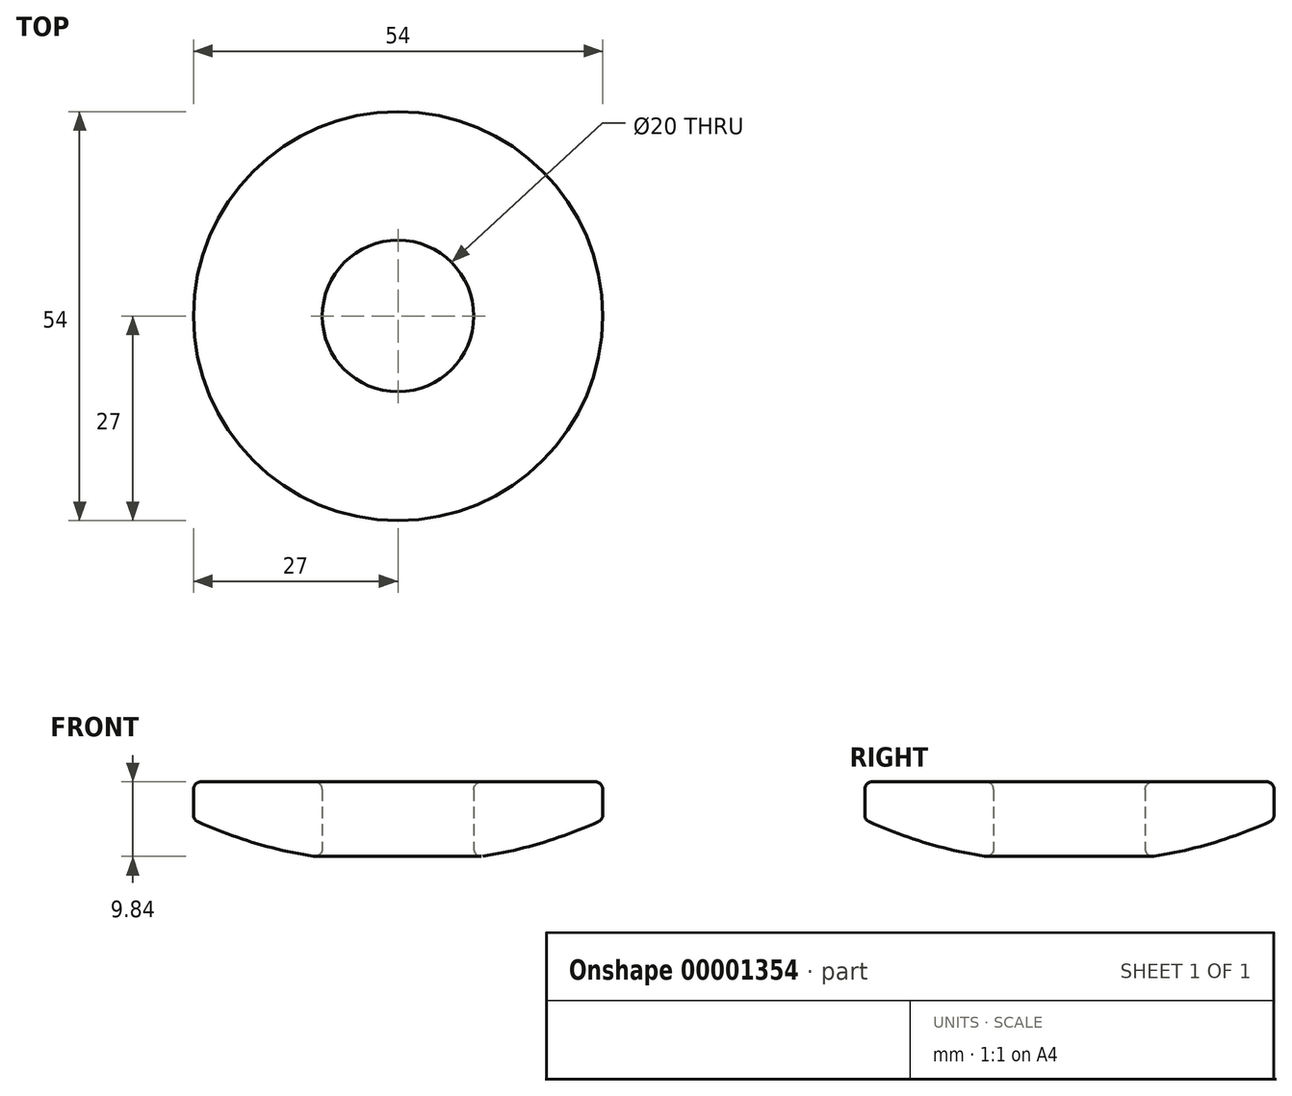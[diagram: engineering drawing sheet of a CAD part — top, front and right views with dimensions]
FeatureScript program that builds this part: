
annotation { "Feature Type Name" : "Feature", "Feature Type Description" : "" }
export const myFeature = defineFeature(function(context is Context, id is Id, definition is map)
    precondition{}
    {
        {
            var Q0;
            Q0=qCreatedBy(makeId("Front.planeOp"),FACE);
            var sketch = newSketch(context, id + "F0", { "sketchPlane" : qUnion([Q0])});
            skLineSegment(sketch, "E0", {"start": v(10, 25) * mm, "end": v(10, 15) * mm});
            skLineSegment(sketch, "E1", {"start": v(10, 25) * mm, "end": v(27, 25) * mm});
            skLineSegment(sketch, "E2", {"start": v(27, 25) * mm, "end": v(27, 20) * mm});
            skLineSegment(sketch, "E3", {"start": v(0, -1.9) * mm, "end": v(0, 16.74) * mm, "construction": true});
            skArc(sketch, "E4", {"start": v(10, 15) * mm, "mid": v(18.69, 16.87) * mm, "end": v(27, 20) * mm});
            skSolve(sketch);
        }
        {
            var Q0;
            Q0 = qSketchRegion(id + "F0", true);
            var Q1;
            Q1=sQuery(id+"F0.wireOp",EDGE,"E3");
            revolve(context, id + "F1", {"entities" : qUnion([Q0]), "axis" : qUnion([Q1]), "revolveType" : RevolveType.FULL});
        }
        {
            var Q0;
            Q0=makeQuery(id+"F1.opRevolve","SWEPT_EDGE",EDGE,{"disambiguationData":[OSD([sQuery(id+"F0.wireOp",EDGE,"E0"),sQuery(id+"F0.wireOp",EDGE,"E1")])]});
            var Q1;
            Q1=makeQuery(id+"F1.opRevolve","SWEPT_EDGE",EDGE,{"disambiguationData":[OSD([sQuery(id+"F0.wireOp",EDGE,"E1"),sQuery(id+"F0.wireOp",EDGE,"E2")])]});
            var Q2;
            Q2=makeQuery(id+"F1.opRevolve","SWEPT_EDGE",EDGE,{"disambiguationData":[OSD([sQuery(id+"F0.wireOp",EDGE,"E2"),sQuery(id+"F0.wireOp",EDGE,"E4")])]});
            var Q3;
            Q3=makeQuery(id+"F1.opRevolve","SWEPT_EDGE",EDGE,{"disambiguationData":[OSD([sQuery(id+"F0.wireOp",EDGE,"E0"),sQuery(id+"F0.wireOp",EDGE,"E4")])]});
            fillet(context, id + "F2", {"entities" : qUnion([Q0, Q1, Q2, Q3]), "radius" : 1 * mm, "tangentPropagation" : true, "allowEdgeOverflow" : false});
        }
    });
